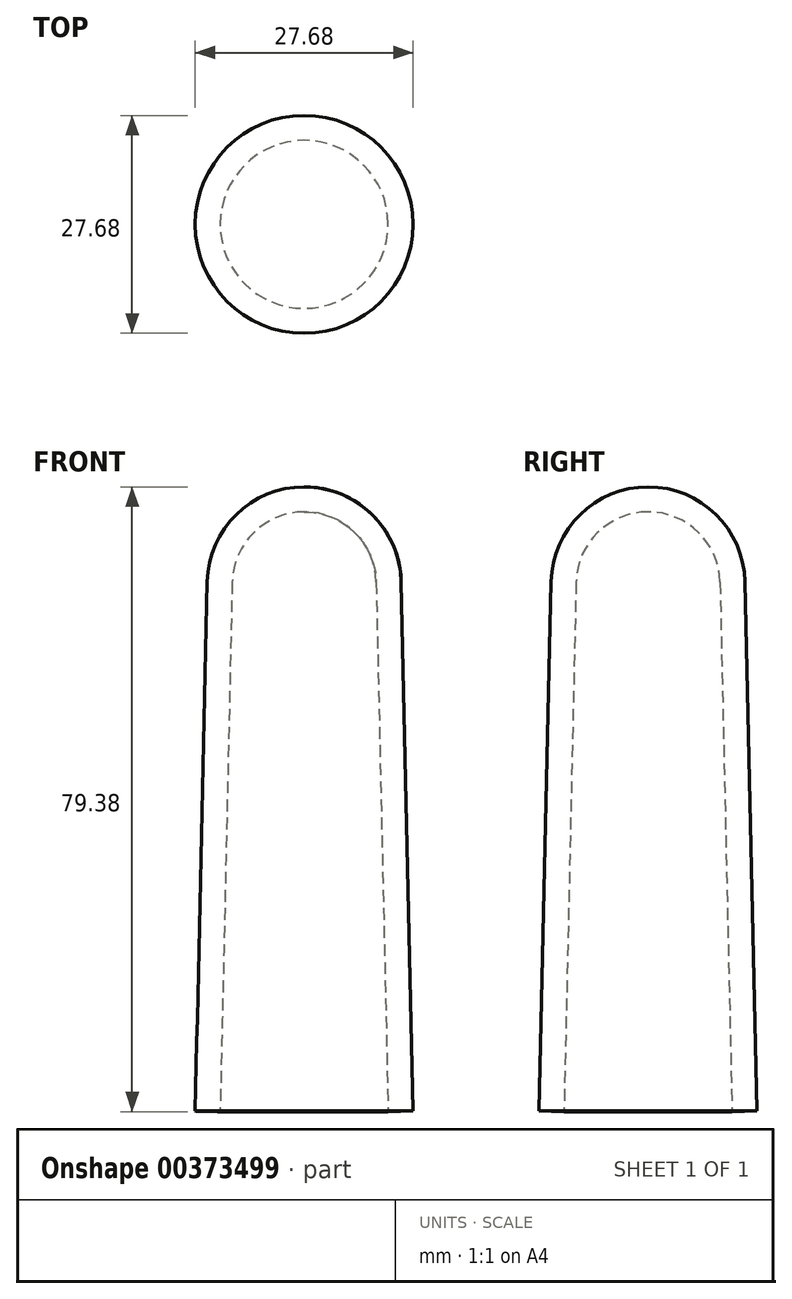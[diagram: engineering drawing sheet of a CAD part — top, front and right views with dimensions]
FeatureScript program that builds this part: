
annotation { "Feature Type Name" : "Feature", "Feature Type Description" : "" }
export const myFeature = defineFeature(function(context is Context, id is Id, definition is map)
    precondition{}
    {
        {
            var Q0;
            Q0=qCreatedBy(makeId("Front.planeOp"),FACE);
            var sketch = newSketch(context, id + "F0", { "sketchPlane" : qUnion([Q0])});
            skLineSegment(sketch, "E0", {"start": v(9.14, 67.26) * mm, "end": v(10.67, 0) * mm});
            skLineSegment(sketch, "E1", {"start": v(10.67, 0) * mm, "end": v(0, 0) * mm, "construction": true});
            skLineSegment(sketch, "E2", {"start": v(0, 0) * mm, "end": v(0, 76.2) * mm, "construction": true});
            skArc(sketch, "E3", {"start": v(9.14, 67.26) * mm, "mid": v(6.4, 73.6) * mm, "end": v(0, 76.2) * mm});
            skArc(sketch, "E4.0", {"start": v(12.32, 67.33) * mm, "mid": v(8.61, 75.86) * mm, "end": v(0, 79.38) * mm});
            skLineSegment(sketch, "E4.1", {"start": v(12.32, 67.33) * mm, "end": v(13.84, 0.07) * mm});
            skLineSegment(sketch, "E5", {"start": v(0, 79.38) * mm, "end": v(0, 76.2) * mm});
            skLineSegment(sketch, "E6", {"start": v(10.67, 0) * mm, "end": v(13.84, 0.07) * mm});
            skSolve(sketch);
        }
        {
            var Q0;
            Q0=qCreatedBy(makeId("Front.planeOp"),FACE);
            var sketch = newSketch(context, id + "F1", { "sketchPlane" : qUnion([Q0])});
            skLineSegment(sketch, "E7", {"start": v(0, -71.48) * mm, "end": v(0, 133.08) * mm});
            skSolve(sketch);
        }
        {
            var Q0;
            Q0 = qSketchRegion(id + "F0", true);
            var Q1;
            Q1=sQuery(id+"F1.wireOp",EDGE,"E7");
            revolve(context, id + "F2", {"entities" : qUnion([Q0]), "axis" : qUnion([Q1]), "revolveType" : RevolveType.FULL});
        }
    });
